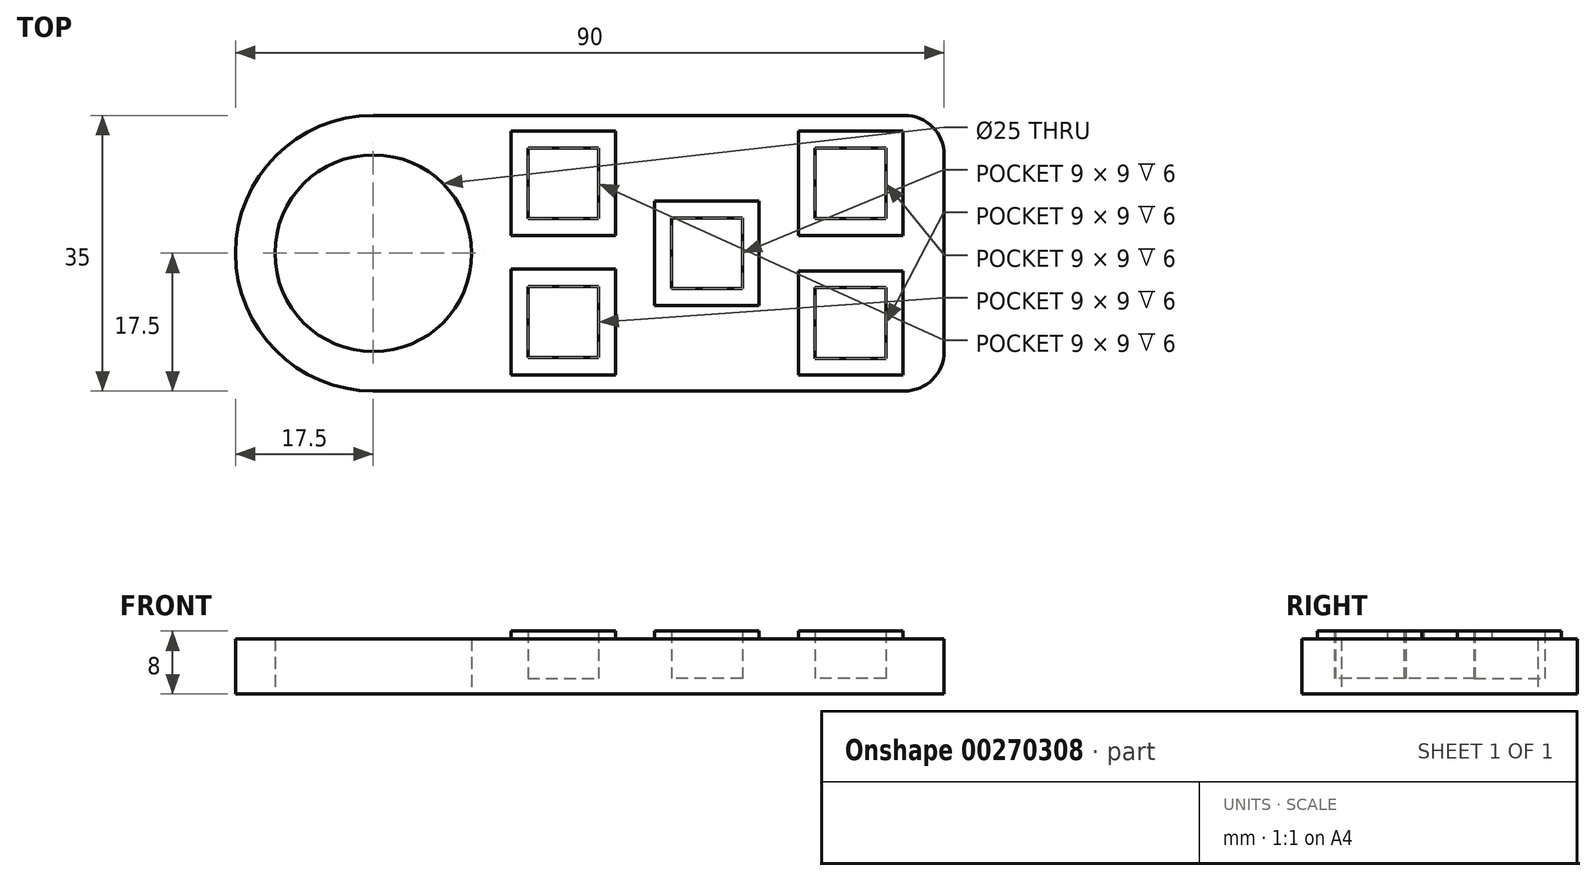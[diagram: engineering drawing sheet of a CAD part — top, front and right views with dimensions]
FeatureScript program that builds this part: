
annotation { "Feature Type Name" : "Feature", "Feature Type Description" : "" }
export const myFeature = defineFeature(function(context is Context, id is Id, definition is map)
    precondition{}
    {
        {
            var Q0;
            Q0=qCreatedBy(makeId("Top.planeOp"),FACE);
            var sketch = newSketch(context, id + "F0", { "sketchPlane" : qUnion([Q0])});
            skLineSegment(sketch, "E0.bottom", {"start": v(17.5, 0) * mm, "end": v(85, 0) * mm});
            skLineSegment(sketch, "E0.top", {"start": v(17.5, 35) * mm, "end": v(85, 35) * mm});
            skLineSegment(sketch, "E0.left", {"start": v(0, 17.5) * mm, "end": v(0, 17.5) * mm});
            skLineSegment(sketch, "E0.right", {"start": v(90, 5) * mm, "end": v(90, 30) * mm});
            skLineSegment(sketch, "E1.bottom", {"start": v(0, 0) * mm, "end": v(17.5, 0) * mm, "construction": true});
            skLineSegment(sketch, "E1.top", {"start": v(0, 17.5) * mm, "end": v(17.5, 17.5) * mm, "construction": true});
            skLineSegment(sketch, "E1.left", {"start": v(0, 0) * mm, "end": v(0, 17.5) * mm, "construction": true});
            skLineSegment(sketch, "E1.right", {"start": v(17.5, 0) * mm, "end": v(17.5, 17.5) * mm, "construction": true});
            skCircle(sketch, "E2", {"center": v(17.5, 17.5) * mm, "radius": 12.5 * mm});
            skPoint(sketch, "E3.visualSharp", {"position": v(0, 0) * mm});
            skArc(sketch, "E3.filletArc", {"start": v(0, 17.5) * mm, "mid": v(5.13, 5.13) * mm, "end": v(17.5, 0) * mm});
            skPoint(sketch, "E4.visualSharp", {"position": v(0, 35) * mm});
            skArc(sketch, "E4.filletArc", {"start": v(17.5, 35) * mm, "mid": v(5.13, 29.87) * mm, "end": v(0, 17.5) * mm});
            skPoint(sketch, "E5.visualSharp", {"position": v(90, 35) * mm});
            skArc(sketch, "E5.filletArc", {"start": v(90, 30) * mm, "mid": v(88.54, 33.54) * mm, "end": v(85, 35) * mm});
            skPoint(sketch, "E6.visualSharp", {"position": v(90, 0) * mm});
            skArc(sketch, "E6.filletArc", {"start": v(85, 0) * mm, "mid": v(88.54, 1.46) * mm, "end": v(90, 5) * mm});
            skSolve(sketch);
        }
        {
            var Q0;
            Q0=makeQuery(id+"F0.imprint","IMPRINT",FACE,{"disambiguationData":[TD([[makeQuery(id+"F0.imprint","IMPRINT",EDGE,{"derivedFrom":sQuery(id+"F0.wireOp",EDGE,"E0.bottom")}),1.0]])]});
            extrude(context, id + "F1", {"entities" : qUnion([Q0]), "depth" : 7 * mm});
        }
        {
            var Q0;
            Q0=makeQuery(id+"F1.opExtrude","CAP_FACE",FACE,{"disambiguationData":[OSD([sQuery(id+"F0.wireOp",EDGE,"E0.bottom"),sQuery(id+"F0.wireOp",EDGE,"E0.top"),sQuery(id+"F0.wireOp",EDGE,"E0.right"),sQuery(id+"F0.wireOp",EDGE,"E2"),sQuery(id+"F0.wireOp",EDGE,"E3.filletArc"),sQuery(id+"F0.wireOp",EDGE,"E4.filletArc"),sQuery(id+"F0.wireOp",EDGE,"E5.filletArc"),sQuery(id+"F0.wireOp",EDGE,"E6.filletArc")])],"isStart":false});
            var sketch = newSketch(context, id + "F2", { "sketchPlane" : qUnion([Q0])});
            skLineSegment(sketch, "E7.bottom", {"start": v(0, 0) * mm, "end": v(35, 0) * mm, "construction": true});
            skLineSegment(sketch, "E7.top", {"start": v(0, 33) * mm, "end": v(35, 33) * mm, "construction": true});
            skLineSegment(sketch, "E7.left", {"start": v(0, 0) * mm, "end": v(0, 33) * mm, "construction": true});
            skLineSegment(sketch, "E7.right", {"start": v(35, 0) * mm, "end": v(35, 33) * mm, "construction": true});
            skLineSegment(sketch, "E8.bottom", {"start": v(35, 33) * mm, "end": v(84.75, 33) * mm, "construction": true});
            skLineSegment(sketch, "E8.top", {"start": v(35, 2) * mm, "end": v(84.75, 2) * mm, "construction": true});
            skLineSegment(sketch, "E8.left", {"start": v(35, 33) * mm, "end": v(35, 2) * mm, "construction": true});
            skLineSegment(sketch, "E8.right", {"start": v(84.75, 33) * mm, "end": v(84.75, 2) * mm, "construction": true});
            skLineSegment(sketch, "E9", {"start": v(35, 33) * mm, "end": v(84.75, 2) * mm, "construction": true});
            skLineSegment(sketch, "E10.bottom", {"start": v(35, 33) * mm, "end": v(48.25, 33) * mm});
            skLineSegment(sketch, "E10.top", {"start": v(35, 19.75) * mm, "end": v(48.25, 19.75) * mm});
            skLineSegment(sketch, "E10.left", {"start": v(35, 33) * mm, "end": v(35, 19.75) * mm});
            skLineSegment(sketch, "E10.right", {"start": v(48.25, 33) * mm, "end": v(48.25, 19.75) * mm});
            skLineSegment(sketch, "E11.bottom", {"start": v(35, 2) * mm, "end": v(48.25, 2) * mm});
            skLineSegment(sketch, "E11.top", {"start": v(35, 15.5) * mm, "end": v(48.25, 15.5) * mm});
            skLineSegment(sketch, "E11.left", {"start": v(35, 2) * mm, "end": v(35, 15.5) * mm});
            skLineSegment(sketch, "E11.right", {"start": v(48.25, 2) * mm, "end": v(48.25, 15.5) * mm});
            skLineSegment(sketch, "E12.bottom", {"start": v(84.75, 33) * mm, "end": v(71.5, 33) * mm});
            skLineSegment(sketch, "E12.top", {"start": v(84.75, 19.75) * mm, "end": v(71.5, 19.75) * mm});
            skLineSegment(sketch, "E12.left", {"start": v(84.75, 33) * mm, "end": v(84.75, 19.75) * mm});
            skLineSegment(sketch, "E12.right", {"start": v(71.5, 33) * mm, "end": v(71.5, 19.75) * mm});
            skLineSegment(sketch, "E13.bottom", {"start": v(84.75, 2) * mm, "end": v(71.5, 2) * mm});
            skLineSegment(sketch, "E13.top", {"start": v(84.75, 15.25) * mm, "end": v(71.5, 15.25) * mm});
            skLineSegment(sketch, "E13.left", {"start": v(84.75, 2) * mm, "end": v(84.75, 15.25) * mm});
            skLineSegment(sketch, "E13.right", {"start": v(71.5, 2) * mm, "end": v(71.5, 15.25) * mm});
            skLineSegment(sketch, "E14.bottom", {"start": v(66.5, 24.13) * mm, "end": v(53.25, 24.13) * mm});
            skLineSegment(sketch, "E14.top", {"start": v(66.5, 10.88) * mm, "end": v(53.25, 10.88) * mm});
            skLineSegment(sketch, "E14.left", {"start": v(66.5, 24.13) * mm, "end": v(66.5, 10.88) * mm});
            skLineSegment(sketch, "E14.right", {"start": v(53.25, 24.13) * mm, "end": v(53.25, 10.88) * mm});
            skPoint(sketch, "E14.middle", {"position": v(59.88, 17.5) * mm});
            skLineSegment(sketch, "E15", {"start": v(48.25, 33) * mm, "end": v(35, 19.75) * mm, "construction": true});
            skLineSegment(sketch, "E16", {"start": v(48.25, 15.5) * mm, "end": v(35, 2) * mm, "construction": true});
            skLineSegment(sketch, "E17", {"start": v(84.75, 33) * mm, "end": v(71.5, 19.75) * mm, "construction": true});
            skLineSegment(sketch, "E18", {"start": v(84.75, 15.25) * mm, "end": v(71.5, 2) * mm, "construction": true});
            skLineSegment(sketch, "E19.bottom", {"start": v(37.13, 21.88) * mm, "end": v(46.13, 21.88) * mm});
            skLineSegment(sketch, "E19.top", {"start": v(37.13, 30.88) * mm, "end": v(46.13, 30.88) * mm});
            skLineSegment(sketch, "E19.left", {"start": v(37.13, 21.88) * mm, "end": v(37.13, 30.88) * mm});
            skLineSegment(sketch, "E19.right", {"start": v(46.13, 21.88) * mm, "end": v(46.13, 30.88) * mm});
            skPoint(sketch, "E19.middle", {"position": v(41.62, 26.38) * mm});
            skLineSegment(sketch, "E20.bottom", {"start": v(37.12, 13.25) * mm, "end": v(46.12, 13.25) * mm});
            skLineSegment(sketch, "E20.top", {"start": v(37.12, 4.25) * mm, "end": v(46.12, 4.25) * mm});
            skLineSegment(sketch, "E20.left", {"start": v(37.12, 13.25) * mm, "end": v(37.12, 4.25) * mm});
            skLineSegment(sketch, "E20.right", {"start": v(46.12, 13.25) * mm, "end": v(46.12, 4.25) * mm});
            skPoint(sketch, "E20.middle", {"position": v(41.62, 8.75) * mm});
            skLineSegment(sketch, "E21.bottom", {"start": v(73.62, 13.12) * mm, "end": v(82.62, 13.12) * mm});
            skLineSegment(sketch, "E21.top", {"start": v(73.62, 4.12) * mm, "end": v(82.62, 4.12) * mm});
            skLineSegment(sketch, "E21.left", {"start": v(73.62, 13.12) * mm, "end": v(73.62, 4.12) * mm});
            skLineSegment(sketch, "E21.right", {"start": v(82.62, 13.12) * mm, "end": v(82.62, 4.12) * mm});
            skPoint(sketch, "E21.middle", {"position": v(78.12, 8.62) * mm});
            skLineSegment(sketch, "E22.bottom", {"start": v(82.63, 21.88) * mm, "end": v(73.63, 21.88) * mm});
            skLineSegment(sketch, "E22.top", {"start": v(82.63, 30.88) * mm, "end": v(73.63, 30.88) * mm});
            skLineSegment(sketch, "E22.left", {"start": v(82.63, 21.88) * mm, "end": v(82.63, 30.88) * mm});
            skLineSegment(sketch, "E22.right", {"start": v(73.63, 21.88) * mm, "end": v(73.63, 30.88) * mm});
            skPoint(sketch, "E22.middle", {"position": v(78.12, 26.38) * mm});
            skLineSegment(sketch, "E23.bottom", {"start": v(64.38, 22) * mm, "end": v(55.38, 22) * mm});
            skLineSegment(sketch, "E23.top", {"start": v(64.38, 13) * mm, "end": v(55.38, 13) * mm});
            skLineSegment(sketch, "E23.left", {"start": v(64.38, 22) * mm, "end": v(64.38, 13) * mm});
            skLineSegment(sketch, "E23.right", {"start": v(55.38, 22) * mm, "end": v(55.38, 13) * mm});
            skSolve(sketch);
        }
        {
            var Q0;
            Q0=makeQuery(id+"F2.imprint","IMPRINT",FACE,{"disambiguationData":[TD([[makeQuery(id+"F2.imprint","IMPRINT",EDGE,{"derivedFrom":sQuery(id+"F2.wireOp",EDGE,"E10.bottom")}),-1.0]])]});
            var Q1;
            Q1=makeQuery(id+"F2.imprint","IMPRINT",FACE,{"disambiguationData":[TD([[makeQuery(id+"F2.imprint","IMPRINT",EDGE,{"derivedFrom":sQuery(id+"F2.wireOp",EDGE,"E11.bottom")}),1.0]])]});
            var Q2;
            Q2=makeQuery(id+"F2.imprint","IMPRINT",FACE,{"disambiguationData":[TD([[makeQuery(id+"F2.imprint","IMPRINT",EDGE,{"derivedFrom":sQuery(id+"F2.wireOp",EDGE,"E14.bottom")}),1.0]])]});
            var Q3;
            Q3=makeQuery(id+"F2.imprint","IMPRINT",FACE,{"disambiguationData":[TD([[makeQuery(id+"F2.imprint","IMPRINT",EDGE,{"derivedFrom":sQuery(id+"F2.wireOp",EDGE,"E13.bottom")}),-1.0]])]});
            var Q4;
            Q4=makeQuery(id+"F2.imprint","IMPRINT",FACE,{"disambiguationData":[TD([[makeQuery(id+"F2.imprint","IMPRINT",EDGE,{"derivedFrom":sQuery(id+"F2.wireOp",EDGE,"E12.bottom")}),1.0]])]});
            extrude(context, id + "F3", {"entities" : qUnion([Q0, Q1, Q2, Q3, Q4]), "operationType" : NewBodyOperationType.ADD, "depth" : 1 * mm});
        }
        {
            var Q0;
            Q0=makeQuery(id+"F2.imprint","IMPRINT",FACE,{"disambiguationData":[TD([[makeQuery(id+"F2.imprint","IMPRINT",EDGE,{"derivedFrom":sQuery(id+"F2.wireOp",EDGE,"E19.bottom")}),1.0]])]});
            var Q1;
            Q1=makeQuery(id+"F2.imprint","IMPRINT",FACE,{"disambiguationData":[TD([[makeQuery(id+"F2.imprint","IMPRINT",EDGE,{"derivedFrom":sQuery(id+"F2.wireOp",EDGE,"E20.bottom")}),-1.0]])]});
            var Q2;
            Q2=makeQuery(id+"F2.imprint","IMPRINT",FACE,{"disambiguationData":[TD([[makeQuery(id+"F2.imprint","IMPRINT",EDGE,{"derivedFrom":sQuery(id+"F2.wireOp",EDGE,"E23.bottom")}),1.0]])]});
            var Q3;
            Q3=makeQuery(id+"F2.imprint","IMPRINT",FACE,{"disambiguationData":[TD([[makeQuery(id+"F2.imprint","IMPRINT",EDGE,{"derivedFrom":sQuery(id+"F2.wireOp",EDGE,"E22.bottom")}),-1.0]])]});
            var Q4;
            Q4=makeQuery(id+"F2.imprint","IMPRINT",FACE,{"disambiguationData":[TD([[makeQuery(id+"F2.imprint","IMPRINT",EDGE,{"derivedFrom":sQuery(id+"F2.wireOp",EDGE,"E21.bottom")}),-1.0]])]});
            extrude(context, id + "F4", {"entities" : qUnion([Q0, Q1, Q2, Q3, Q4]), "operationType" : NewBodyOperationType.REMOVE, "oppositeDirection" : true, "depth" : 5 * mm});
        }
    });
